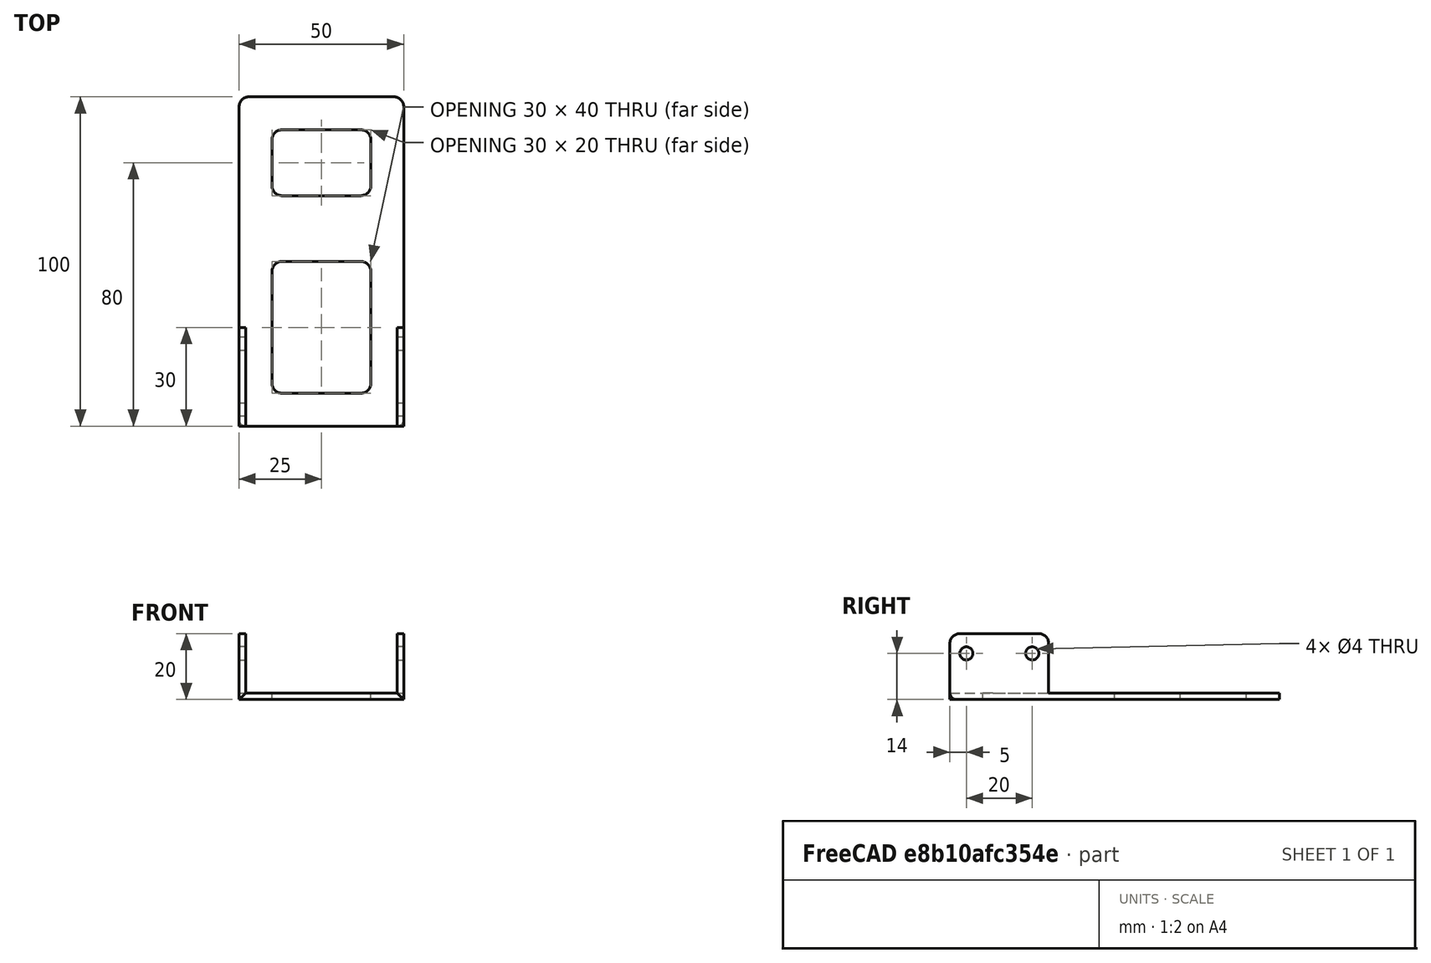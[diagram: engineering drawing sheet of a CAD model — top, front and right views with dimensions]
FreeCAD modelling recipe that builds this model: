
FCSTD DOCUMENT  (FreeCAD 0.21R33694 (Git))
Label: OJT1_T12P02_peça
License: All rights reserved
LicenseURL: http://en.wikipedia.org/wiki/All_rights_reserved
objects: Part::Fillet×8, Part::Cut×6, Part::Box×5, Part::Cylinder×4, Part::Fuse×2
note: 25 computed .brp shape members not serialized (recipe doc carries the construction recipe); baked Part::Feature solids carry a one-line shape summary decoded from their .brp

FEATURE [Part::Box] Box004  label="Cube004"
  AttacherType = Attacher::AttachEngine3D
  Height = 2
  Length = 50
  Width = 100
FEATURE [Part::Fillet] Fillet005
  Base = -> Box004
  Edges = 2 edges r=2: [Edge1,Edge5]
FEATURE [Part::Fillet] Fillet006  label="base"
  Base = -> Fillet005
  Edges = 2 edges r=3: [Edge4,Edge13]
FEATURE [Part::Box] Box005  label="Cube005"
  AttacherType = Attacher::AttachEngine3D
  Height = 2
  Length = 30
  Width = 40
FEATURE [Part::Fillet] Fillet007  label="forat1"
  Base = -> Box005
  Edges = 4 edges r=3: [Edge1,Edge3,Edge5,Edge7]
  Placement = pos=(10,10,0) rot=(0,0,1;0rad)
FEATURE [Part::Box] Box006  label="Cube006"
  AttacherType = Attacher::AttachEngine3D
  Height = 2
  Length = 30
  Width = 20
FEATURE [Part::Fillet] Fillet008  label="forat2"
  Base = -> Box006
  Edges = 4 edges r=3: [Edge1,Edge3,Edge5,Edge7]
  Placement = pos=(10,70,0) rot=(0,0,1;0rad)
FEATURE [Part::Cut] Cut004
  Base = -> Fillet006
  Refine = true
  Tool = -> Fillet007
FEATURE [Part::Cut] Cut005  label="Peça_principal"
  Base = -> Cut004
  Refine = true
  Tool = -> Fillet008
FEATURE [Part::Box] Box007  label="Cube007"
  AttacherType = Attacher::AttachEngine3D
  Height = 20
  Length = 2
  Width = 30
FEATURE [Part::Fillet] Fillet009
  Base = -> Box007
  Edges = 2 edges r=2: [Edge9,Edge11]
FEATURE [Part::Fillet] Fillet010  label="peça_subprincipal"
  Base = -> Fillet009
  Edges = 2 edges r=3: [Edge9,Edge12]
FEATURE [Part::Cylinder] Cylinder002
  Angle = 360
  AttacherType = Attacher::AttachEngine3D
  FirstAngle = 0
  Height = 10
  Placement = pos=(0,5,14) rot=(0,1,0;1.5708rad)
  Radius = 2
  SecondAngle = 0
FEATURE [Part::Cylinder] Cylinder003
  Angle = 360
  AttacherType = Attacher::AttachEngine3D
  FirstAngle = 0
  Height = 10
  Placement = pos=(0,25,14) rot=(0,1,0;1.5708rad)
  Radius = 2
  SecondAngle = 0
FEATURE [Part::Cut] Cut006
  Base = -> Fillet010
  Refine = true
  Tool = -> Cylinder002
FEATURE [Part::Cut] Cut007  label="mini_peça"
  Base = -> Cut006
  Refine = true
  Tool = -> Cylinder003
FEATURE [Part::Box] Box008  label="Cube008"
  AttacherType = Attacher::AttachEngine3D
  Height = 20
  Length = 2
  Width = 30
FEATURE [Part::Cylinder] Cylinder004
  Angle = 360
  AttacherType = Attacher::AttachEngine3D
  FirstAngle = 0
  Height = 10
  Placement = pos=(0,5,14) rot=(0,1,0;1.5708rad)
  Radius = 2
  SecondAngle = 0
FEATURE [Part::Cylinder] Cylinder005
  Angle = 360
  AttacherType = Attacher::AttachEngine3D
  FirstAngle = 0
  Height = 10
  Placement = pos=(0,25,14) rot=(0,1,0;1.5708rad)
  Radius = 2
  SecondAngle = 0
FEATURE [Part::Fillet] Fillet011
  Base = -> Box008
  Edges = 2 edges r=2: [Edge9,Edge11]
FEATURE [Part::Fillet] Fillet012  label="peça_subprincipal001"
  Base = -> Fillet011
  Edges = 2 edges r=3: [Edge9,Edge12]
FEATURE [Part::Cut] Cut008
  Base = -> Fillet012
  Refine = true
  Tool = -> Cylinder004
FEATURE [Part::Cut] Cut009  label="mini_peça001"
  Base = -> Cut008
  Placement = pos=(48,0,0) rot=(0,0,1;0rad)
  Refine = true
  Tool = -> Cylinder005
FEATURE [Part::Fuse] Fusion
  Base = -> Cut005
  Refine = true
  Tool = -> Cut007
FEATURE [Part::Fuse] Fusion001  label="peça"
  Base = -> Cut009
  Refine = true
  Tool = -> Fusion
